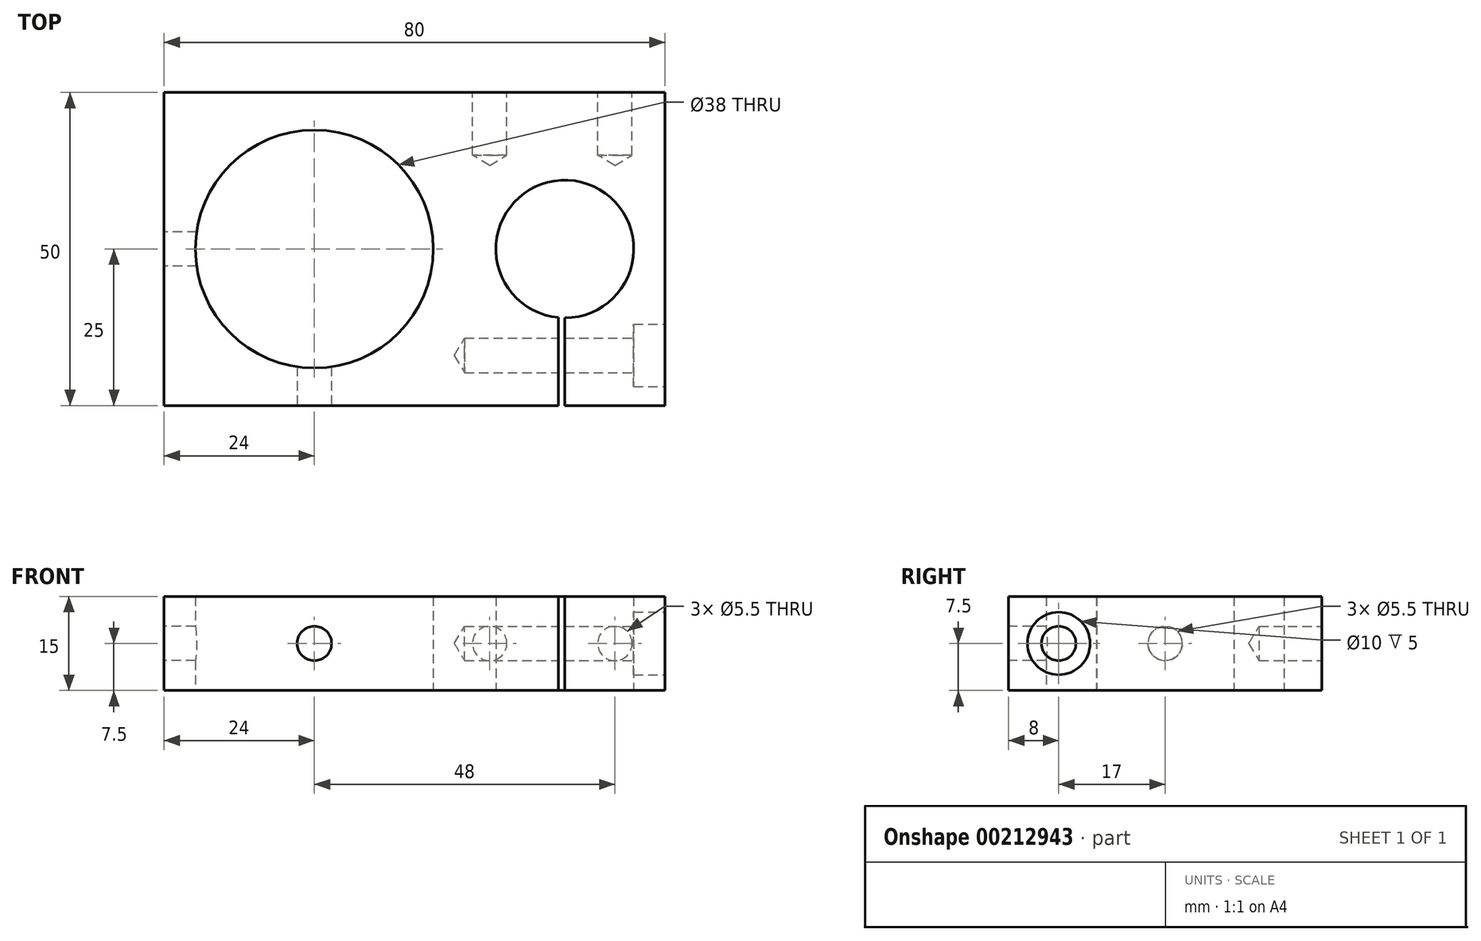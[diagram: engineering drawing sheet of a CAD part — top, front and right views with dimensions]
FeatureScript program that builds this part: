
annotation { "Feature Type Name" : "Feature", "Feature Type Description" : "" }
export const myFeature = defineFeature(function(context is Context, id is Id, definition is map)
    precondition{}
    {
        {
            var Q0;
            Q0=qCreatedBy(makeId("Top.planeOp"),FACE);
            var sketch = newSketch(context, id + "F0", { "sketchPlane" : qUnion([Q0])});
            skLineSegment(sketch, "E0.bottom", {"start": v(-40, 25) * mm, "end": v(40, 25) * mm});
            skLineSegment(sketch, "E0.top", {"start": v(-40, -25) * mm, "end": v(40, -25) * mm});
            skLineSegment(sketch, "E0.left", {"start": v(-40, 25) * mm, "end": v(-40, -25) * mm});
            skLineSegment(sketch, "E0.right", {"start": v(40, 25) * mm, "end": v(40, -25) * mm});
            skCircle(sketch, "E1", {"center": v(-16, 0) * mm, "radius": 19 * mm});
            skCircle(sketch, "E2", {"center": v(24, 0) * mm, "radius": 11 * mm});
            skSolve(sketch);
        }
        {
            var Q0;
            Q0 = qSketchRegion(id + "F0", true);
            extrude(context, id + "F1", {"entities" : qUnion([Q0]), "depth" : 15 * mm});
        }
        {
            var Q0;
            Q0=makeQuery(id+"F1.opExtrude","CAP_FACE",FACE,{"disambiguationData":[OSD([sQuery(id+"F0.wireOp",EDGE,"E0.bottom"),sQuery(id+"F0.wireOp",EDGE,"E0.top"),sQuery(id+"F0.wireOp",EDGE,"E0.left"),sQuery(id+"F0.wireOp",EDGE,"E0.right"),sQuery(id+"F0.wireOp",EDGE,"E1"),sQuery(id+"F0.wireOp",EDGE,"E2")])],"isStart":false});
            var sketch = newSketch(context, id + "F2", { "sketchPlane" : qUnion([Q0])});
            skLineSegment(sketch, "E3.bottom", {"start": v(23, -25) * mm, "end": v(24, -25) * mm});
            skLineSegment(sketch, "E3.top", {"start": v(23, -10) * mm, "end": v(24, -10) * mm});
            skLineSegment(sketch, "E3.left", {"start": v(23, -25) * mm, "end": v(23, -10) * mm});
            skLineSegment(sketch, "E3.right", {"start": v(24, -25) * mm, "end": v(24, -10) * mm});
            skSolve(sketch);
        }
        {
            var Q0;
            Q0 = qSketchRegion(id + "F2", true);
            extrude(context, id + "F3", {"entities" : qUnion([Q0]), "operationType" : NewBodyOperationType.REMOVE, "oppositeDirection" : true, "depth" : 25 * mm});
        }
        {
            var Q0;
            Q0=makeQuery(id+"F1.opExtrude","SWEPT_FACE",FACE,{"disambiguationData":[OSD([sQuery(id+"F0.wireOp",EDGE,"E0.right")])]});
            var sketch = newSketch(context, id + "F4", { "sketchPlane" : qUnion([Q0])});
            skPoint(sketch, "E4", {"position": v(-17, 7.5) * mm});
            skSolve(sketch);
        }
        {
            var Q0;
            Q0=sQuery(id+"F4.wireOp",VERTEX,"E4");
            var Q1;
            Q1=makeQuery(id+"F1.opExtrude","SWEPT_BODY",BODY,{"disambiguationData":[OSD([sQuery(id+"F0.wireOp",EDGE,"E0.bottom"),sQuery(id+"F0.wireOp",EDGE,"E0.top"),sQuery(id+"F0.wireOp",EDGE,"E0.left"),sQuery(id+"F0.wireOp",EDGE,"E0.right"),sQuery(id+"F0.wireOp",EDGE,"E1"),sQuery(id+"F0.wireOp",EDGE,"E2")])]});
            hole(context, id + "F5", {"style" : HoleStyle.C_BORE, "endStyle" : HoleEndStyle.BLIND, "holeDiameter" : 5.5 * mm, "cBoreDiameter" : 10 * mm, "cBoreDepth" : 5 * mm, "holeDepth" : 18 * mm, "locations" : qUnion([Q0]), "scope" : qUnion([Q1])});
        }
        {
            var Q0;
            Q0=makeQuery(id+"F3.boolean.opBoolean","COPY",FACE,{"derivedFrom":makeQuery(id+"F3.opExtrude","SWEPT_FACE",FACE,{"disambiguationData":[OSD([sQuery(id+"F2.wireOp",EDGE,"E3.left")])]})});
            var sketch = newSketch(context, id + "F6", { "sketchPlane" : qUnion([Q0])});
            skPoint(sketch, "E5", {"position": v(-17, 7.5) * mm});
            skSolve(sketch);
        }
        {
            var Q0;
            Q0=sQuery(id+"F6.wireOp",VERTEX,"E5");
            var Q1;
            Q1=makeQuery(id+"F1.opExtrude","SWEPT_BODY",BODY,{"disambiguationData":[OSD([sQuery(id+"F0.wireOp",EDGE,"E0.bottom"),sQuery(id+"F0.wireOp",EDGE,"E0.top"),sQuery(id+"F0.wireOp",EDGE,"E0.left"),sQuery(id+"F0.wireOp",EDGE,"E0.right"),sQuery(id+"F0.wireOp",EDGE,"E1"),sQuery(id+"F0.wireOp",EDGE,"E2")])]});
            hole(context, id + "F7", {"style" : HoleStyle.SIMPLE, "endStyle" : HoleEndStyle.BLIND, "standardTappedOrClearance" : lookupTablePath({ "standard" : "ISO", "fit" : "Normal", "size" : "M5", "type" : "Clearance" }), "standardBlindInLast" : lookupTablePath({ "fit" : "Standard", "standard" : "ISO", "size" : "M5", "type" : "Clearance" }), "holeDiameter" : 5.5 * mm, "holeDepth" : 15 * mm, "locations" : qUnion([Q0]), "scope" : qUnion([Q1])});
        }
        {
            var Q0;
            {var subQ3=sQuery(id+"F0.wireOp",EDGE,"E0.left");var subQ4=sQuery(id+"F0.wireOp",EDGE,"E0.top");Q0=makeQuery(id+"F3.boolean.opBoolean","SPLIT",FACE,{"disambiguationData":[TD([makeQuery(id+"F1.opExtrude","SWEPT_FACE",FACE,{"disambiguationData":[OSD([subQ3])]})])],"derivedFrom":makeQuery(id+"F1.opExtrude","SWEPT_FACE",FACE,{"disambiguationData":[OSD([subQ4])]})});}
            var sketch = newSketch(context, id + "F8", { "sketchPlane" : qUnion([Q0])});
            skPoint(sketch, "E6", {"position": v(-16, 7.5) * mm});
            skSolve(sketch);
        }
        {
            var Q0;
            Q0=sQuery(id+"F8.wireOp",VERTEX,"E6");
            var Q1;
            Q1=makeQuery(id+"F1.opExtrude","SWEPT_BODY",BODY,{"disambiguationData":[OSD([sQuery(id+"F0.wireOp",EDGE,"E0.bottom"),sQuery(id+"F0.wireOp",EDGE,"E0.top"),sQuery(id+"F0.wireOp",EDGE,"E0.left"),sQuery(id+"F0.wireOp",EDGE,"E0.right"),sQuery(id+"F0.wireOp",EDGE,"E1"),sQuery(id+"F0.wireOp",EDGE,"E2")])]});
            hole(context, id + "F9", {"style" : HoleStyle.SIMPLE, "endStyle" : HoleEndStyle.BLIND, "standardTappedOrClearance" : lookupTablePath({ "standard" : "ISO", "fit" : "Normal", "size" : "M5", "type" : "Clearance" }), "standardBlindInLast" : lookupTablePath({ "fit" : "Standard", "standard" : "ISO", "size" : "M5", "type" : "Clearance" }), "holeDiameter" : 5.5 * mm, "holeDepth" : 15 * mm, "locations" : qUnion([Q0]), "scope" : qUnion([Q1])});
        }
        {
            var Q0;
            Q0=makeQuery(id+"F1.opExtrude","SWEPT_FACE",FACE,{"disambiguationData":[OSD([sQuery(id+"F0.wireOp",EDGE,"E0.left")])]});
            var sketch = newSketch(context, id + "F10", { "sketchPlane" : qUnion([Q0])});
            skPoint(sketch, "E7", {"position": v(0, 7.5) * mm});
            skPoint(sketch, "E7.positionSnap0", {"position": v(25, 7.5) * mm});
            skSolve(sketch);
        }
        {
            var Q0;
            Q0=sQuery(id+"F10.wireOp",VERTEX,"E7");
            var Q1;
            Q1=makeQuery(id+"F1.opExtrude","SWEPT_BODY",BODY,{"disambiguationData":[OSD([sQuery(id+"F0.wireOp",EDGE,"E0.bottom"),sQuery(id+"F0.wireOp",EDGE,"E0.top"),sQuery(id+"F0.wireOp",EDGE,"E0.left"),sQuery(id+"F0.wireOp",EDGE,"E0.right"),sQuery(id+"F0.wireOp",EDGE,"E1"),sQuery(id+"F0.wireOp",EDGE,"E2")])]});
            hole(context, id + "F11", {"style" : HoleStyle.SIMPLE, "endStyle" : HoleEndStyle.BLIND, "standardTappedOrClearance" : lookupTablePath({ "standard" : "ISO", "fit" : "Normal", "size" : "M5", "type" : "Clearance" }), "standardBlindInLast" : lookupTablePath({ "fit" : "Standard", "standard" : "ISO", "size" : "M5", "type" : "Clearance" }), "holeDiameter" : 5.5 * mm, "holeDepth" : 15 * mm, "locations" : qUnion([Q0]), "scope" : qUnion([Q1])});
        }
        {
            var Q0;
            Q0=makeQuery(id+"F1.opExtrude","SWEPT_FACE",FACE,{"disambiguationData":[OSD([sQuery(id+"F0.wireOp",EDGE,"E0.bottom")])]});
            var sketch = newSketch(context, id + "F12", { "sketchPlane" : qUnion([Q0])});
            skPoint(sketch, "E8", {"position": v(-32, 7.5) * mm});
            skPoint(sketch, "E8.positionSnap0", {"position": v(-40, 7.5) * mm});
            skPoint(sketch, "E9", {"position": v(-12, 7.5) * mm});
            skSolve(sketch);
        }
        {
            var Q0;
            Q0=sQuery(id+"F12.wireOp",VERTEX,"E8");
            var Q1;
            Q1=sQuery(id+"F12.wireOp",VERTEX,"E9");
            var Q2;
            Q2=makeQuery(id+"F1.opExtrude","SWEPT_BODY",BODY,{"disambiguationData":[OSD([sQuery(id+"F0.wireOp",EDGE,"E0.bottom"),sQuery(id+"F0.wireOp",EDGE,"E0.top"),sQuery(id+"F0.wireOp",EDGE,"E0.left"),sQuery(id+"F0.wireOp",EDGE,"E0.right"),sQuery(id+"F0.wireOp",EDGE,"E1"),sQuery(id+"F0.wireOp",EDGE,"E2")])]});
            hole(context, id + "F13", {"style" : HoleStyle.SIMPLE, "endStyle" : HoleEndStyle.BLIND, "standardTappedOrClearance" : lookupTablePath({ "standard" : "ISO", "fit" : "Normal", "size" : "M5", "type" : "Clearance" }), "standardBlindInLast" : lookupTablePath({ "fit" : "Standard", "standard" : "ISO", "size" : "M5", "type" : "Clearance" }), "holeDiameter" : 5.5 * mm, "holeDepth" : 10 * mm, "locations" : qUnion([Q0, Q1]), "scope" : qUnion([Q2])});
        }
    });
